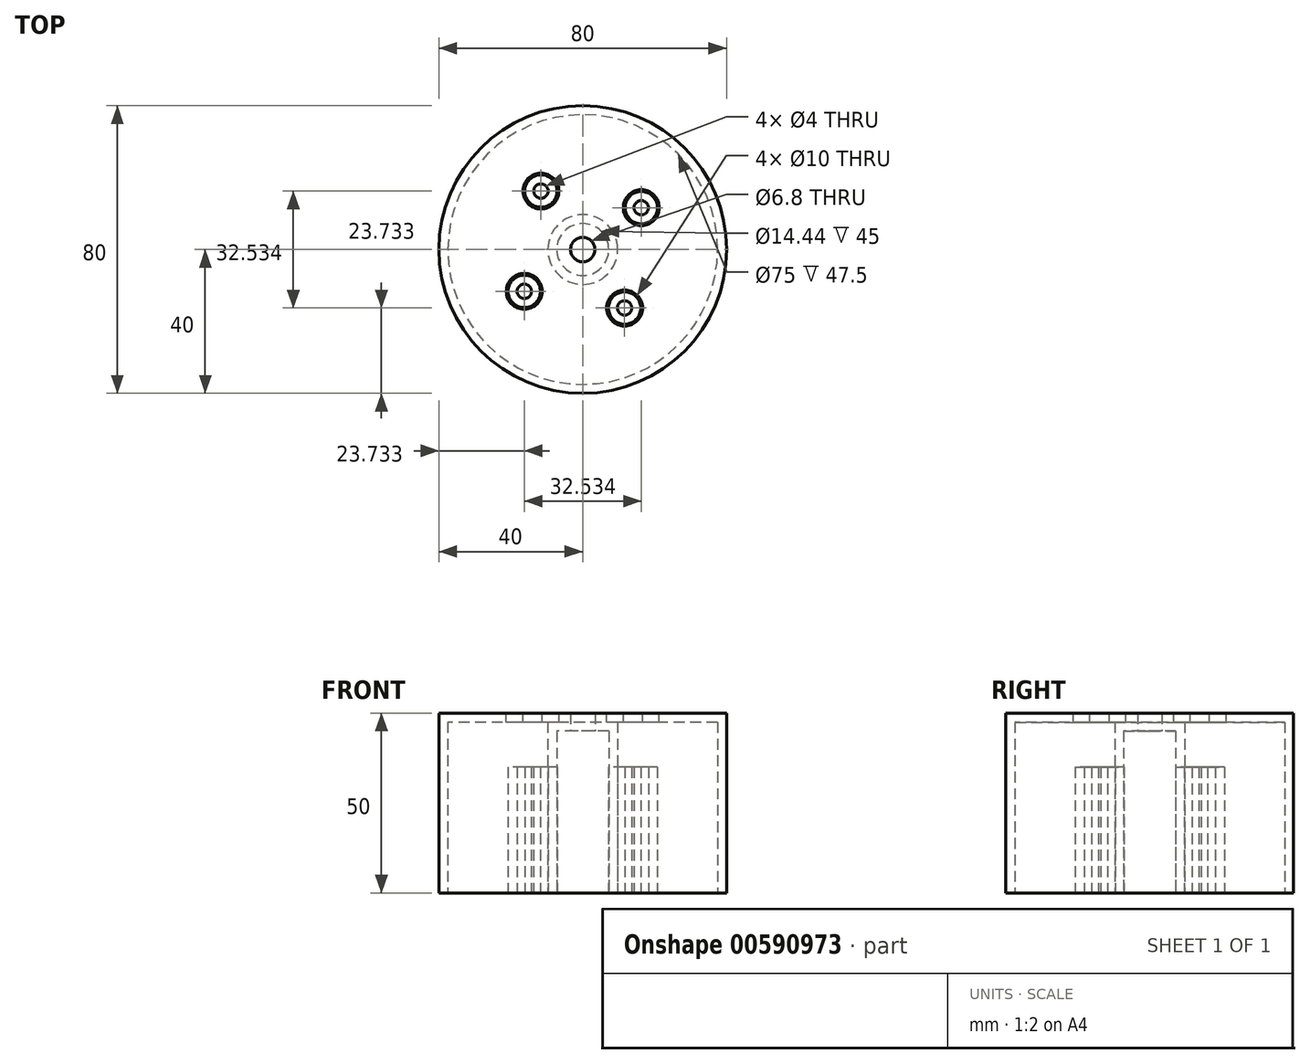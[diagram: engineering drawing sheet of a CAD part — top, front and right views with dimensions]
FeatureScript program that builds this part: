
annotation { "Feature Type Name" : "Feature", "Feature Type Description" : "" }
export const myFeature = defineFeature(function(context is Context, id is Id, definition is map)
    precondition{}
    {
        {
            var Q0;
            Q0=qCreatedBy(makeId("Top.planeOp"),FACE);
            var sketch = newSketch(context, id + "F0", { "sketchPlane" : qUnion([Q0])});
            skCircle(sketch, "E0", {"center": v(0, 0) * mm, "radius": 40 * mm});
            skLineSegment(sketch, "E1", {"start": v(0, 0) * mm, "end": v(32.53, 23.27) * mm, "construction": true});
            skLineSegment(sketch, "E2", {"start": v(16.27, 11.64) * mm, "end": v(0, 0) * mm, "construction": true});
            skCircle(sketch, "E3", {"center": v(16.27, 11.64) * mm, "radius": 2 * mm});
            skLineSegment(sketch, "E4", {"start": v(32.53, 23.27) * mm, "end": v(-32.53, -23.27) * mm, "construction": true});
            skLineSegment(sketch, "E5", {"start": v(-32.53, -23.27) * mm, "end": v(-16.27, -11.64) * mm, "construction": true});
            skCircle(sketch, "E6", {"center": v(-16.27, -11.64) * mm, "radius": 2 * mm});
            skLineSegment(sketch, "E7", {"start": v(0, 0) * mm, "end": v(23.27, -32.53) * mm, "construction": true});
            skLineSegment(sketch, "E8", {"start": v(23.27, -32.53) * mm, "end": v(-23.27, 32.53) * mm, "construction": true});
            skLineSegment(sketch, "E9", {"start": v(-23.27, 32.53) * mm, "end": v(-11.64, 16.27) * mm, "construction": true});
            skLineSegment(sketch, "E10", {"start": v(11.64, -16.27) * mm, "end": v(0, 0) * mm, "construction": true});
            skCircle(sketch, "E11", {"center": v(-11.64, 16.27) * mm, "radius": 2 * mm});
            skCircle(sketch, "E12", {"center": v(11.64, -16.27) * mm, "radius": 2 * mm});
            skCircle(sketch, "E13", {"center": v(0, 0) * mm, "radius": 3.4 * mm});
            skSolve(sketch);
        }
        {
            var Q0;
            Q0=qSketchRegion(id+"F0",true);
            extrude(context, id + "F1", {"entities" : qUnion([Q0]), "depth" : 50 * mm});
        }
        {
            var Q0;
            Q0=qCreatedBy(makeId("Top.planeOp"),FACE);
            var sketch = newSketch(context, id + "F2", { "sketchPlane" : qUnion([Q0])});
            skCircle(sketch, "E14", {"center": v(0, 0) * mm, "radius": 7.22 * mm});
            skSolve(sketch);
        }
        {
            var Q0;
            Q0=qSketchRegion(id+"F2",true);
            extrude(context, id + "F3", {"entities" : qUnion([Q0]), "operationType" : NewBodyOperationType.REMOVE, "depth" : 45 * mm});
        }
        {
            var Q0;
            Q0=makeQuery(id+"F1.opExtrude","CAP_FACE",FACE,{"disambiguationData":[OSD([sQuery(id+"F0.wireOp",EDGE,"E0"),sQuery(id+"F0.wireOp",EDGE,"E3"),sQuery(id+"F0.wireOp",EDGE,"E6"),sQuery(id+"F0.wireOp",EDGE,"E11"),sQuery(id+"F0.wireOp",EDGE,"E12"),sQuery(id+"F0.wireOp",EDGE,"E13")])],"isStart":false});
            var sketch = newSketch(context, id + "F4", { "sketchPlane" : qUnion([Q0])});
            skCircle(sketch, "E15", {"center": v(-11.64, 16.27) * mm, "radius": 5 * mm});
            skCircle(sketch, "E16", {"center": v(16.27, 11.64) * mm, "radius": 5 * mm});
            skCircle(sketch, "E17", {"center": v(11.64, -16.27) * mm, "radius": 5 * mm});
            skCircle(sketch, "E18", {"center": v(-16.27, -11.64) * mm, "radius": 5 * mm});
            skSolve(sketch);
        }
        {
            var Q0;
            Q0=qSketchRegion(id+"F4",true);
            extrude(context, id + "F5", {"entities" : qUnion([Q0]), "oppositeDirection" : true, "depth" : 10 * mm});
        }
        {
            var Q0;
            Q0=makeQuery(id+"F1.opExtrude","CAP_FACE",FACE,{"disambiguationData":[OSD([sQuery(id+"F0.wireOp",EDGE,"E0"),sQuery(id+"F0.wireOp",EDGE,"E3"),sQuery(id+"F0.wireOp",EDGE,"E6"),sQuery(id+"F0.wireOp",EDGE,"E11"),sQuery(id+"F0.wireOp",EDGE,"E12"),sQuery(id+"F0.wireOp",EDGE,"E13")])],"isStart":true});
            shell(context, id + "F6", {"entities" : qUnion([Q0]), "thickness" : 2.5 * mm});
        }
        {
            var Q0;
            Q0=makeQuery(id+"F5.opExtrude","CAP_FACE",FACE,{"disambiguationData":[OSD([sQuery(id+"F4.wireOp",EDGE,"E15")])],"isStart":true});
            var Q1;
            Q1=makeQuery(id+"F5.opExtrude","CAP_FACE",FACE,{"disambiguationData":[OSD([sQuery(id+"F4.wireOp",EDGE,"E17")])],"isStart":true});
            var Q2;
            Q2=makeQuery(id+"F5.opExtrude","CAP_FACE",FACE,{"disambiguationData":[OSD([sQuery(id+"F4.wireOp",EDGE,"E16")])],"isStart":true});
            var Q3;
            Q3=makeQuery(id+"F5.opExtrude","CAP_FACE",FACE,{"disambiguationData":[OSD([sQuery(id+"F4.wireOp",EDGE,"E18")])],"isStart":true});
            extrude(context, id + "F7", {"entities" : qUnion([Q0, Q1, Q2, Q3]), "operationType" : NewBodyOperationType.REMOVE, "oppositeDirection" : true, "depth" : 15 * mm});
        }
    });
